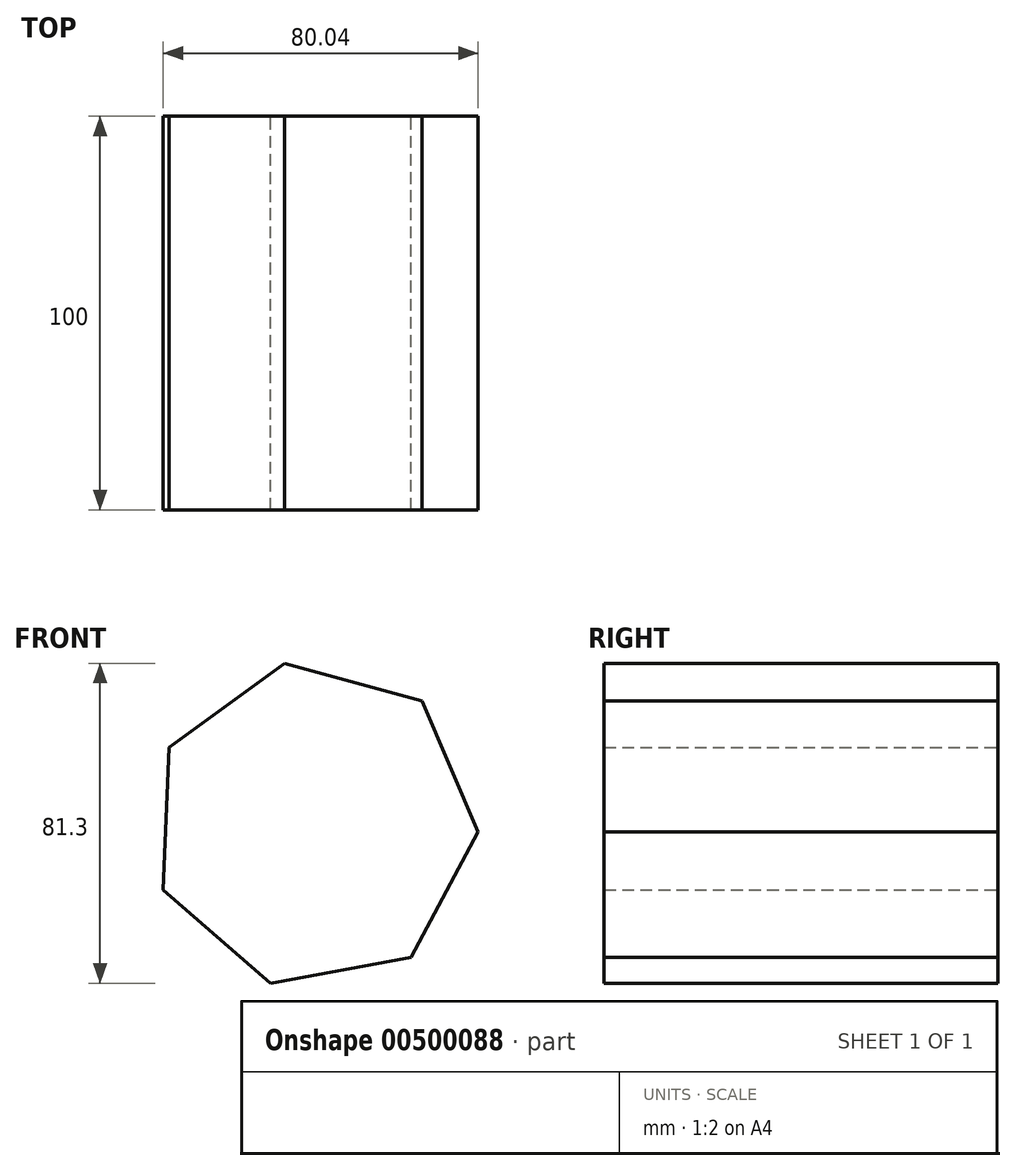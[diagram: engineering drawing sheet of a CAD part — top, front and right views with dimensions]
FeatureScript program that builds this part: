
annotation { "Feature Type Name" : "Feature", "Feature Type Description" : "" }
export const myFeature = defineFeature(function(context is Context, id is Id, definition is map)
    precondition{}
    {
        {
            var Q0;
            Q0=qCreatedBy(makeId("Front.planeOp"),FACE);
            var sketch = newSketch(context, id + "F0", { "sketchPlane" : qUnion([Q0])});
            skCircle(sketch, "E0.cCircle", {"center": v(-34.4, -34.25) * mm, "radius": 41.73 * mm, "construction": true});
            skLineSegment(sketch, "E0.0", {"start": v(-7, -2.77) * mm, "end": v(7.3, -36.04) * mm});
            skLineSegment(sketch, "E0.1", {"start": v(7.3, -36.04) * mm, "end": v(-9.8, -67.96) * mm});
            skLineSegment(sketch, "E0.2", {"start": v(-9.8, -67.96) * mm, "end": v(-45.42, -74.5) * mm});
            skLineSegment(sketch, "E0.3", {"start": v(-45.42, -74.5) * mm, "end": v(-72.74, -50.72) * mm});
            skLineSegment(sketch, "E0.4", {"start": v(-72.74, -50.72) * mm, "end": v(-71.18, -14.54) * mm});
            skLineSegment(sketch, "E0.5", {"start": v(-71.18, -14.54) * mm, "end": v(-41.92, 6.8) * mm});
            skLineSegment(sketch, "E0.6", {"start": v(-41.92, 6.8) * mm, "end": v(-7, -2.77) * mm});
            skSolve(sketch);
        }
        {
            var Q0;
            Q0=makeQuery(id+"F0.imprint","IMPRINT",FACE,{"disambiguationData":[TD([[makeQuery(id+"F0.imprint","IMPRINT",EDGE,{"derivedFrom":sQuery(id+"F0.wireOp",EDGE,"E0.0")}),-1.0]])]});
            extrude(context, id + "F1", {"entities" : qUnion([Q0]), "endBound" : BoundingType.SYMMETRIC, "depth" : 100 * mm});
        }
    });
